# Revit family: NBS_WallgateLtd_WCFlshngVlves_PBA050-51-1
name_source: partatom
category: Plumbing Fixtures
revit_build: Autodesk Revit 2014 (Build: 20130709_2115(x64)
units: mm (PartAtom-declared; Revit-internal decimal feet)

## types (2) — shared parameters
AssetType = Fixed
BodyMaterial = Stainless steel
CableLength = 4000 mm
Description = Electronic activation dual flush single WC piezo touch button
DurationUnit = year
Features = Anti-ligature design, highly vandal-resistant
Finish = Stainless steel
HasIntegralShutOffDevice = No
IfcExportAs = IfcValveType
IfcExportType = FLUSHING
IsHighPressure = No
ManufacturerName = Wallgate Ltd
ManufacturerURL = www.wallgate.com
NBSCertification = www.nationalbimlibrary.com/cert/5ppuv1fx
NBSDescription = WC flushing valves
NBSReference = 45-35-70/389
NominalHeight = 65 mm
NominalWidth = 65 mm
Operation = Piezo push button
ProductInformation = www.wallgate.com/document-centre/docmenu-washroom-controls/docmenu-controls-piezo-activation/doccat-piezo-activation-buttons
Size = 21.0
TestPressure = 0.0
ThirdPartyCertification = Ministry of Justice Safer Cell Approval
Uniclass2 = 45-31-93/491
ValveMechanism = Unset
ValveOperation = Other
Version = 1
WarrantyDurationParts = 1
WarrantyDurationUnit = year
WaterSupplyFittingMaterial = NBS_Concept
zero-valued in all types: CloseOffRating, FlowCoefficient, FlushingRate, WorkingPressure

## per-type parameters (varying)
| type | BIMObjectName | Name | NominalLength | WallThicknessOptions |
| PBA050-1 | NBS_WallgateLtd_WCFlushingValves_PBA050-1 | WCFlushingValves_PBA050-1_WallgateLtd | 98 mm | Minimum 25 mm (with spacer) |
| PBA051-1 | NBS_WallgateLtd_WCFlushingValves_PBA051-1 | WCFlushingValves_PBA051-1_Wallgate | 172 mm | 95-165 mm |

note: column(s) folded — value = type name in every type: ModelNumber

## geometry (parser evidence)
native form markers: Sweep x3
no freeform markers — native parametric forms only
